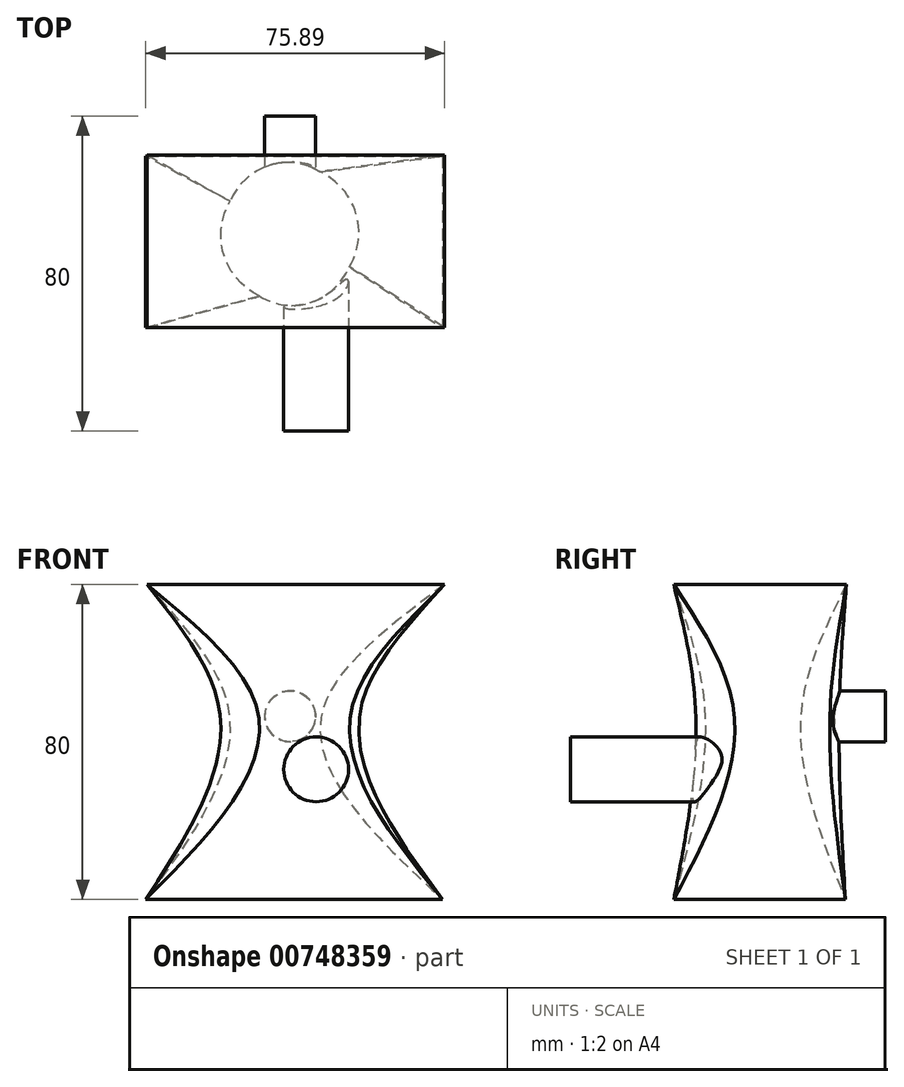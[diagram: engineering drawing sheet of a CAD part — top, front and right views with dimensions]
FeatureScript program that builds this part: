
annotation { "Feature Type Name" : "Feature", "Feature Type Description" : "" }
export const myFeature = defineFeature(function(context is Context, id is Id, definition is map)
    precondition{}
    {
        {
            var Q0;
            Q0=qCreatedBy(makeId("Top.planeOp"),FACE);
            var sketch = newSketch(context, id + "F0", { "sketchPlane" : qUnion([Q0])});
            skLineSegment(sketch, "E0.bottom", {"start": v(-36.68, 19.82) * mm, "end": v(38.65, 19.82) * mm});
            skLineSegment(sketch, "E0.top", {"start": v(-36.68, -23.75) * mm, "end": v(38.65, -23.75) * mm});
            skLineSegment(sketch, "E0.left", {"start": v(-36.68, 19.82) * mm, "end": v(-36.68, -23.75) * mm});
            skLineSegment(sketch, "E0.right", {"start": v(38.65, 19.82) * mm, "end": v(38.65, -23.75) * mm});
            skSolve(sketch);
        }
        {
            var Q0;
            Q0=qCreatedBy(makeId("Top.planeOp"),FACE);
            cPlane(context, id + "F1", {"entities" : qUnion([Q0]), "cplaneType" : CPlaneType.OFFSET, "offset" : 50 * mm, "width" : 150 * mm, "height" : 150 * mm});
        }
        {
            var Q0;
            Q0=qCreatedBy(makeId("Top.planeOp"),FACE);
            cPlane(context, id + "F2", {"entities" : qUnion([Q0]), "cplaneType" : CPlaneType.OFFSET, "offset" : 80 * mm, "width" : 150 * mm, "height" : 150 * mm});
        }
        {
            var Q0;
            Q0=qCreatedBy(id+"F1.planeOp",FACE);
            var sketch = newSketch(context, id + "F3", { "sketchPlane" : qUnion([Q0])});
            skCircle(sketch, "E1", {"center": v(0, 0) * mm, "radius": 18.32 * mm});
            skSolve(sketch);
        }
        {
            var Q0;
            Q0=qCreatedBy(id+"F2.planeOp",FACE);
            var sketch = newSketch(context, id + "F4", { "sketchPlane" : qUnion([Q0])});
            skLineSegment(sketch, "E2.bottom", {"start": v(-36.4, 20.1) * mm, "end": v(39.21, 20.1) * mm});
            skLineSegment(sketch, "E2.top", {"start": v(-36.4, -23.75) * mm, "end": v(39.21, -23.75) * mm});
            skLineSegment(sketch, "E2.left", {"start": v(-36.4, 20.1) * mm, "end": v(-36.4, -23.75) * mm});
            skLineSegment(sketch, "E2.right", {"start": v(39.21, 20.1) * mm, "end": v(39.21, -23.75) * mm});
            skSolve(sketch);
        }
        {
            var Q0;
            Q0=makeQuery(id+"F4.imprint","IMPRINT",FACE,{"disambiguationData":[TD([[makeQuery(id+"F4.imprint","IMPRINT",EDGE,{"derivedFrom":sQuery(id+"F4.wireOp",EDGE,"E2.bottom")}),-1.0]])]});
            var Q1;
            Q1=makeQuery(id+"F3.imprint","IMPRINT",FACE,{"disambiguationData":[TD([[makeQuery(id+"F3.imprint","IMPRINT",EDGE,{"derivedFrom":sQuery(id+"F3.wireOp",EDGE,"E1")}),1.0]])]});
            var Q2;
            Q2=makeQuery(id+"F0.imprint","IMPRINT",FACE,{"disambiguationData":[TD([[makeQuery(id+"F0.imprint","IMPRINT",EDGE,{"derivedFrom":sQuery(id+"F0.wireOp",EDGE,"E0.bottom")}),-1.0]])]});
            loft(context, id + "F5", {"sheetProfilesArray" : [{ "sheetProfileEntities" : qUnion([Q0]) }, { "sheetProfileEntities" : qUnion([Q1]) }, { "sheetProfileEntities" : qUnion([Q2]) }]});
        }
        {
            var Q0;
            Q0=qCreatedBy(makeId("Front.planeOp"),FACE);
            var sketch = newSketch(context, id + "F6", { "sketchPlane" : qUnion([Q0])});
            skCircle(sketch, "E3", {"center": v(0, 46.52) * mm, "radius": 6.46 * mm});
            skSolve(sketch);
        }
        {
            var Q0;
            Q0 = qSketchRegion(id + "F6", true);
            extrude(context, id + "F7", {"entities" : qUnion([Q0]), "operationType" : NewBodyOperationType.ADD, "oppositeDirection" : true, "depth" : 30 * mm, "offsetDistance" : 25 * mm});
        }
        {
            var Q0;
            Q0=qCreatedBy(makeId("Front.planeOp"),FACE);
            cPlane(context, id + "F8", {"entities" : qUnion([Q0]), "cplaneType" : CPlaneType.OFFSET, "offset" : 50 * mm, "width" : 150 * mm, "height" : 150 * mm});
        }
        {
            var Q0;
            Q0=qCreatedBy(id+"F8.planeOp",FACE);
            var sketch = newSketch(context, id + "F9", { "sketchPlane" : qUnion([Q0])});
            skCircle(sketch, "E4", {"center": v(6.6, 33.03) * mm, "radius": 8.23 * mm});
            skSolve(sketch);
        }
        {
            var Q0;
            Q0=makeQuery(id+"F9.imprint","IMPRINT",FACE,{"disambiguationData":[TD([[makeQuery(id+"F9.imprint","IMPRINT",EDGE,{"derivedFrom":sQuery(id+"F9.wireOp",EDGE,"E4")}),1.0]])]});
            extrude(context, id + "F10", {"entities" : qUnion([Q0]), "operationType" : NewBodyOperationType.ADD, "oppositeDirection" : true, "depth" : 50 * mm, "offsetDistance" : 25 * mm});
        }
    });
